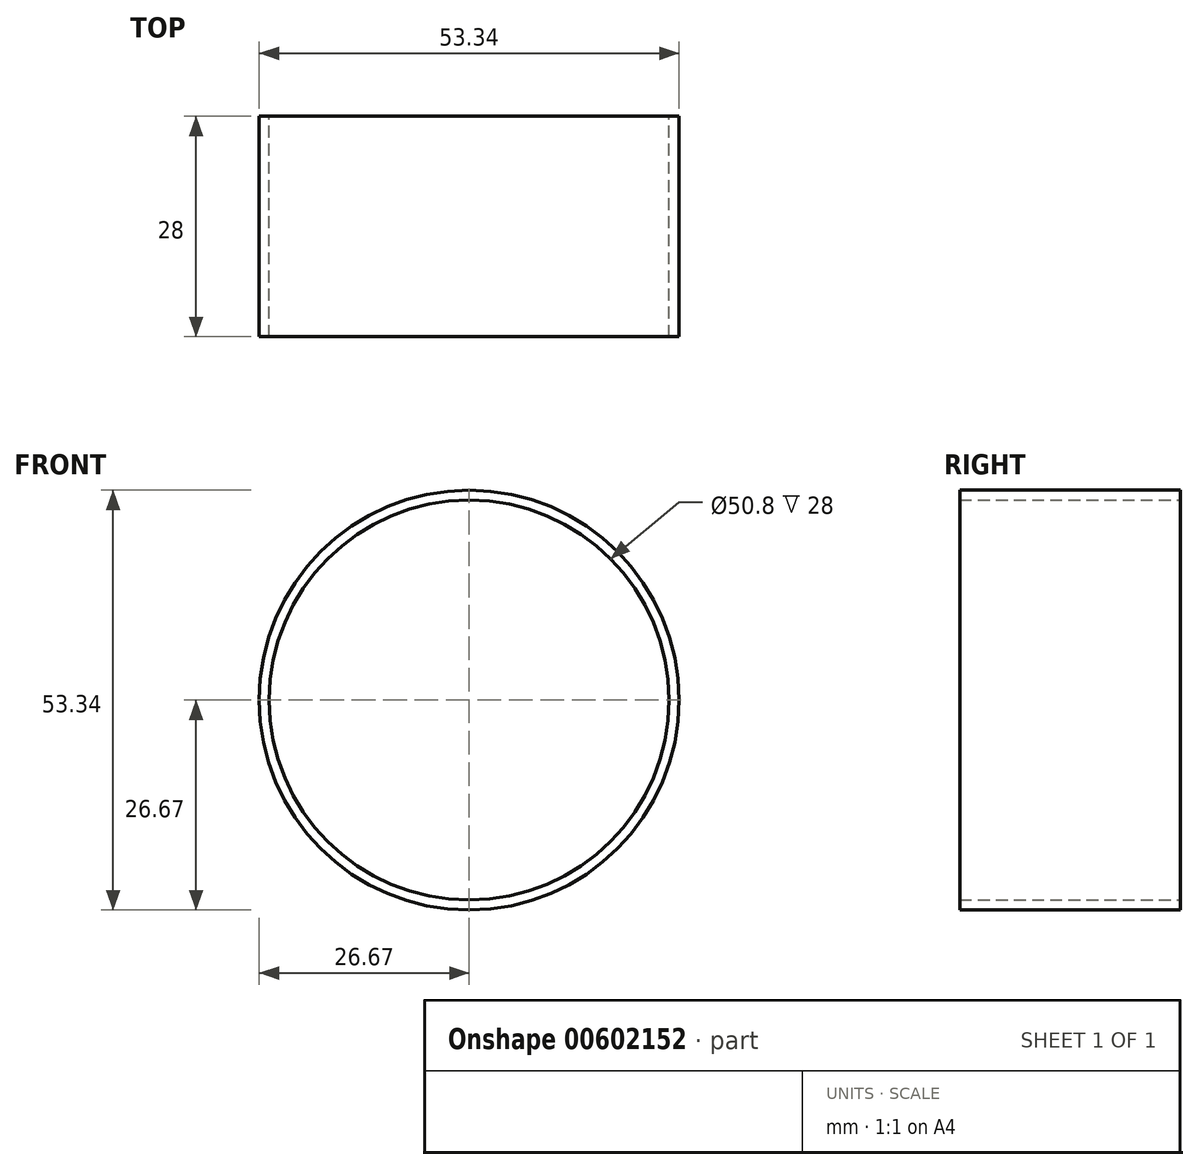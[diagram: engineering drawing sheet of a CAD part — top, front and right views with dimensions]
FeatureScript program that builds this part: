
annotation { "Feature Type Name" : "Feature", "Feature Type Description" : "" }
export const myFeature = defineFeature(function(context is Context, id is Id, definition is map)
    precondition{}
    {
        {
            var Q0;
            Q0=qCreatedBy(makeId("Front.planeOp"),FACE);
            var sketch = newSketch(context, id + "F0", { "sketchPlane" : qUnion([Q0])});
            skCircle(sketch, "E0", {"center": v(0, 0) * mm, "radius": 26.67 * mm});
            skSolve(sketch);
        }
        {
            var Q0;
            Q0=makeQuery(id+"F0.imprint","IMPRINT",FACE,{"disambiguationData":[TD([[makeQuery(id+"F0.imprint","IMPRINT",EDGE,{"derivedFrom":sQuery(id+"F0.wireOp",EDGE,"E0")}),1.0]])]});
            var sketch = newSketch(context, id + "F1", { "sketchPlane" : qUnion([Q0])});
            skCircle(sketch, "E1", {"center": v(0, 0) * mm, "radius": 25.4 * mm});
            skSolve(sketch);
        }
        {
            var Q0;
            Q0=makeQuery(id+"F0.imprint","IMPRINT",FACE,{"disambiguationData":[TD([[makeQuery(id+"F0.imprint","IMPRINT",EDGE,{"derivedFrom":sQuery(id+"F0.wireOp",EDGE,"E0")}),1.0]])]});
            var Q1;
            Q1=sQuery(id+"F0.wireOp",EDGE,"E0");
            var Q2;
            Q2=sQuery(id+"F1.wireOp",EDGE,"E1");
            extrude(context, id + "F2", {"entities" : qUnion([Q0]), "surfaceEntities" : qUnion([Q1, Q2]), "depth" : 28 * mm, "offsetDistance" : 25.4 * mm});
        }
        {
            var Q0;
            Q0=qSketchRegion(id+"F1",true);
            extrude(context, id + "F3", {"entities" : qUnion([Q0]), "operationType" : NewBodyOperationType.REMOVE, "depth" : 31.32 * mm, "offsetDistance" : 25.4 * mm});
        }
    });
